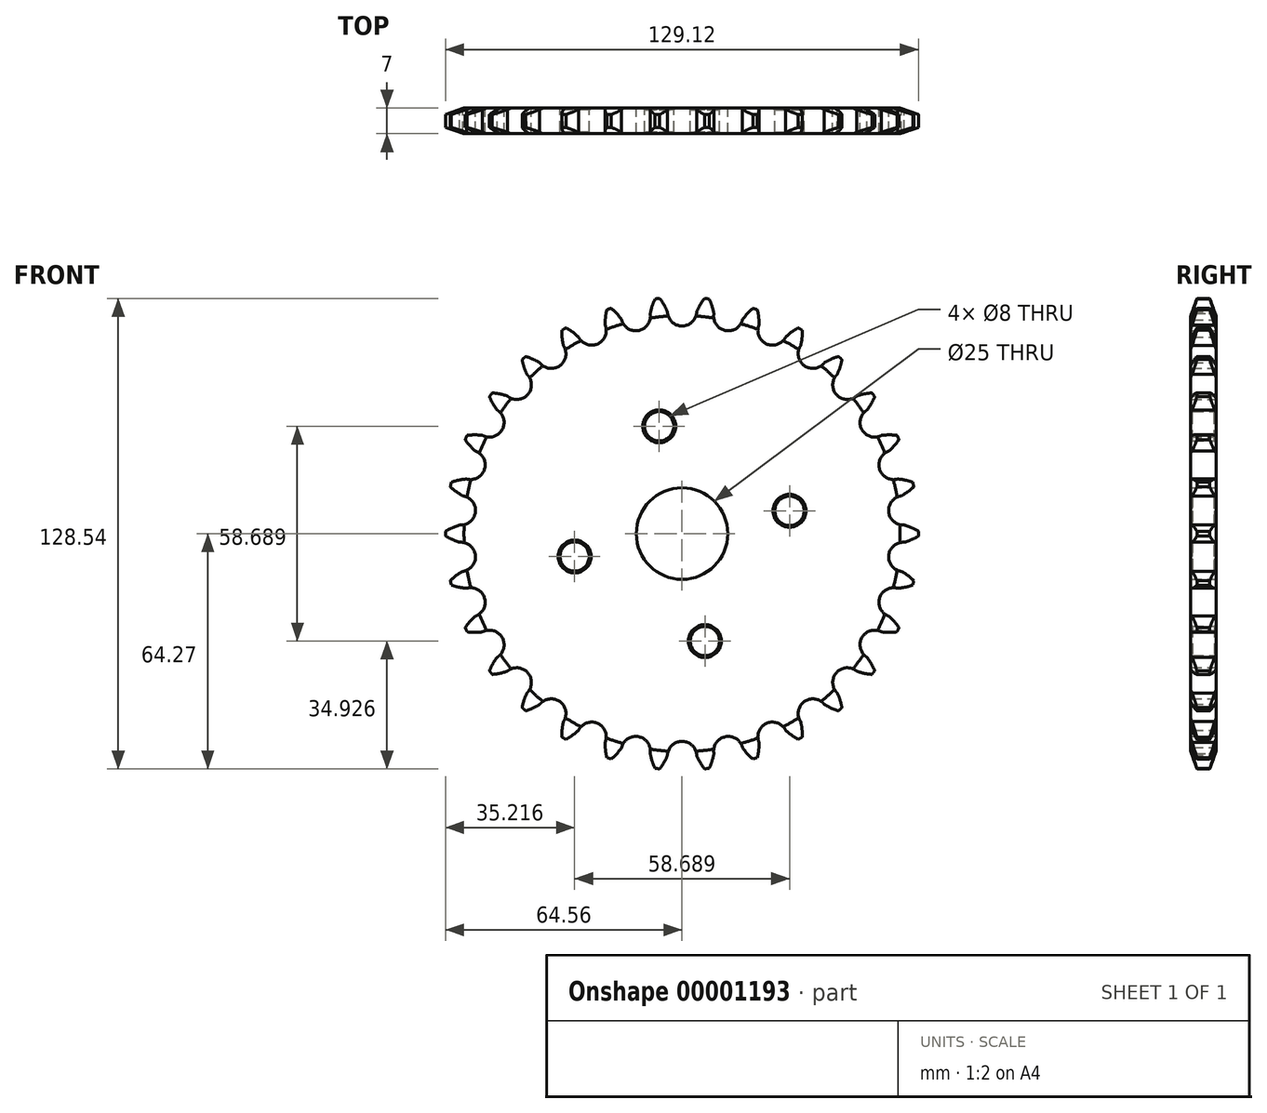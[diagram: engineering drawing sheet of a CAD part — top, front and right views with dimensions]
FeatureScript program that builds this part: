
annotation { "Feature Type Name" : "Feature", "Feature Type Description" : "" }
export const myFeature = defineFeature(function(context is Context, id is Id, definition is map)
    precondition{}
    {
        {
            var Q0;
            Q0=qCreatedBy(makeId("Front.planeOp"),FACE);
            var sketch = newSketch(context, id + "F0", { "sketchPlane" : qUnion([Q0])});
            skCircle(sketch, "E0", {"center": v(0, 0) * mm, "radius": 12.5 * mm});
            skCircle(sketch, "E1", {"center": v(0, 0) * mm, "radius": 64.56 * mm});
            skLineSegment(sketch, "E2", {"start": v(0, 0) * mm, "end": v(-13.42, 63.15) * mm});
            skCircle(sketch, "E3", {"center": v(0, 0) * mm, "radius": 60.75 * mm});
            skArc(sketch, "E4", {"start": v(-7.39, 64.13) * mm, "mid": v(-8.17, 62.17) * mm, "end": v(-8.7, 60.12) * mm});
            skArc(sketch, "E5.0.MirrorCS", {"start": v(-19.34, 61.6) * mm, "mid": v(-17.82, 60.12) * mm, "end": v(-16.51, 58.46) * mm});
            skArc(sketch, "E6", {"start": v(-16.51, 58.46) * mm, "mid": v(-11.8, 55.5) * mm, "end": v(-8.7, 60.12) * mm});
            skLineSegment(sketch, "E7", {"start": v(-12.63, 59.42) * mm, "end": v(0, 60.75) * mm, "construction": true});
            skLineSegment(sketch, "E8", {"start": v(-19.34, 61.6) * mm, "end": v(-16.51, 58.46) * mm, "construction": true});
            skLineSegment(sketch, "E9", {"start": v(-8.7, 60.12) * mm, "end": v(-7.39, 64.13) * mm, "construction": true});
            skCircle(sketch, "E10", {"center": v(-6.24, 29.34) * mm, "radius": 4 * mm});
            skSolve(sketch);
        }
        {
            var Q0;
            {var subQ5=sQuery(id+"F0.wireOp",EDGE,"E0");Q0=makeQuery(id+"F0.imprint","IMPRINT",FACE,{"disambiguationData":[TD([[makeQuery(id+"F0.imprint","IMPRINT",EDGE,{"derivedFrom":subQ5}),-1.0]])]});}
            var Q1;
            {var subQ1=sQuery(id+"F0.wireOp",EDGE,"E4");Q1=makeQuery(id+"F0.imprint","IMPRINT",FACE,{"disambiguationData":[TD([[makeQuery(id+"F0.imprint","IMPRINT",EDGE,{"derivedFrom":subQ1}),1.0]])]});}
            extrude(context, id + "F1", {"entities" : qUnion([Q0, Q1]), "endBound" : BoundingType.SYMMETRIC, "depth" : 7 * mm});
        }
        {
            var Q0;
            Q0=makeQuery(id+"F1.opExtrude","CAP_EDGE",EDGE,{"disambiguationData":[OSD([sQuery(id+"F0.wireOp",EDGE,"E1")])],"isStart":false});
            var Q1;
            Q1=makeQuery(id+"F1.opExtrude","CAP_EDGE",EDGE,{"disambiguationData":[OSD([sQuery(id+"F0.wireOp",EDGE,"E1")])],"isStart":true});
            chamfer(context, id + "F2", {"entities" : qUnion([Q0, Q1]), "chamferType" : ChamferType.TWO_OFFSETS, "width1" : 5 * mm, "oppositeDirection" : false, "width2" : 1.73 * mm, "tangentPropagation" : true});
        }
        {
            var Q0;
            Q0=makeQuery(id+"F1.opExtrude","SWEPT_FACE",FACE,{"disambiguationData":[OSD([sQuery(id+"F0.wireOp",EDGE,"E5.0.MirrorCS")])]});
            var Q1;
            Q1=makeQuery(id+"F1.opExtrude","SWEPT_FACE",FACE,{"disambiguationData":[OSD([sQuery(id+"F0.wireOp",EDGE,"E6")])]});
            var Q2;
            Q2=makeQuery(id+"F1.opExtrude","SWEPT_FACE",FACE,{"disambiguationData":[OSD([sQuery(id+"F0.wireOp",EDGE,"E4")])]});
            var Q3;
            Q3=makeQuery(id+"F1.opExtrude","SWEPT_FACE",FACE,{"disambiguationData":[OSD([sQuery(id+"F0.wireOp",EDGE,"E0")])]});
            circularPattern(context, id + "F3", {"faces" : qUnion([Q0, Q1, Q2]), "axis" : qUnion([Q3]), "angle" : 360 * degree, "instanceCount" : 30, "equalSpace" : true, "patternType" : PatternType.FACE});
        }
        {
            var Q0;
            Q0=makeQuery(id+"F1.opExtrude","CAP_EDGE",EDGE,{"disambiguationData":[OSD([sQuery(id+"F0.wireOp",EDGE,"E10")])],"isStart":true});
            var Q1;
            Q1=makeQuery(id+"F1.opExtrude","CAP_EDGE",EDGE,{"disambiguationData":[OSD([sQuery(id+"F0.wireOp",EDGE,"E10")])],"isStart":false});
            chamfer(context, id + "F4", {"entities" : qUnion([Q0, Q1]), "width" : .5 * mm, "tangentPropagation" : true});
        }
        {
            var Q0;
            Q0=makeQuery(id+"F1.opExtrude","SWEPT_FACE",FACE,{"disambiguationData":[OSD([sQuery(id+"F0.wireOp",EDGE,"E10")])]});
            var Q1;
            {var subQ0=sQuery(id+"F0.wireOp",EDGE,"E10");Q1=makeQuery(id+"F4.opChamfer","BLEND_FACE",FACE,{"disambiguationData":[OSD([subQ0]),TDD([makeQuery(id+"F1.opExtrude","CAP_EDGE",EDGE,{"disambiguationData":[OSD([subQ0])],"isStart":true})])]});}
            var Q2;
            {var subQ0=sQuery(id+"F0.wireOp",EDGE,"E10");Q2=makeQuery(id+"F4.opChamfer","BLEND_FACE",FACE,{"disambiguationData":[OSD([subQ0]),TDD([makeQuery(id+"F1.opExtrude","CAP_EDGE",EDGE,{"disambiguationData":[OSD([subQ0])],"isStart":false})])]});}
            var Q3;
            Q3=makeQuery(id+"F1.opExtrude","SWEPT_FACE",FACE,{"disambiguationData":[OSD([sQuery(id+"F0.wireOp",EDGE,"E0")])]});
            circularPattern(context, id + "F5", {"faces" : qUnion([Q0, Q1, Q2]), "axis" : qUnion([Q3]), "angle" : 360 * degree, "instanceCount" : 4, "equalSpace" : true, "patternType" : PatternType.FACE});
        }
    });
